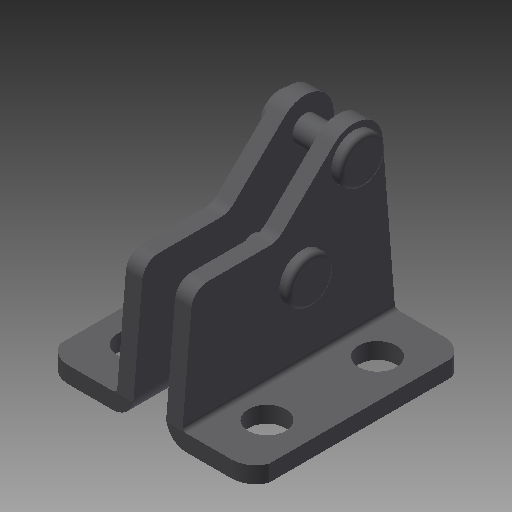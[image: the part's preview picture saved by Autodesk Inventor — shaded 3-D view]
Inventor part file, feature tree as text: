
AUTODESK INVENTOR PART (.ipt)
format: ipt  version: 2018 (Build 220112000, 112)  size: 232,960 bytes
history: native  units: mm
features: other x14, sketch x10, extrude x8, revolve x2
ambient origin geometry x8: Origin, YZ Plane, XZ Plane, XY Plane, X Axis, Y Axis, Z Axis, Center Point
bodies: Solid1 (feature_tree)
feature tree (34):
  extrude  "Extrusion1"  TaperAngle=360.0deg  [1 undecoded]
  revolve  "Revolution1"  [1 undecoded]
  revolve  "Revolution2"  [1 undecoded]
  extrude  "Extrusion2"  Depth=2.0mm TaperAngle=0.0deg
  extrude  "Extrusion3"  Depth=2.0mm TaperAngle=0.0deg
  extrude  "Extrusion4"  [1 undecoded]
  extrude  "Extrusion5"  [1 undecoded]
  extrude  "Extrusion6"  [1 undecoded]
  extrude  "Extrusion7"  [1 undecoded]
  extrude  "Extrusion8"  [1 undecoded]
  other  "WF1_XY"
  other  "WF1_YZ"
  other  "WF1_ZX"
  other  "WF1_X"
  other  "WF1_Y"
  other  "WF1_Z"
  other  "WF1_Center"
  other  "WF2_XY"
  other  "WF2_YZ"
  other  "WF2_ZX"
  other  "WF2_X"
  other  "WF2_Y"
  other  "WF2_Z"
  other  "WF2_Center"
  sketch  "Skizze_1"  dims[d0=26.0mm d1=0.0mm d2=360.0deg]
  sketch  "Skizze_2"  dims[d6=100.0mm d7=0.0mm d8=2.0mm d9=0.0mm]
  sketch  "Skizze_3"  dims[d14=2.0mm d15=0.0mm d16=2.0mm d17=0.0mm]
  sketch  "Skizze_5"
  sketch  "Skizze_6"
  sketch  "Skizze_7"
  sketch  "Skizze_8_ALT_Drilling_1"  dims[d3=360.0deg d4=26.0mm d5=0.0mm]
  sketch  "Skizze_9_ALT_Drilling_2"  dims[d10=2.0mm d11=0.0mm d12=2.0mm d13=0.0mm]
  sketch  "Skizze_10_ALT_Drilling_3"
  sketch  "Skizze_11_ALT_Drilling_4"
note: 8 required parameter values undecoded (feature->parameter linkage not recoverable at this tier; creation-order binding heuristic only, values carry confidence <= 0.55)